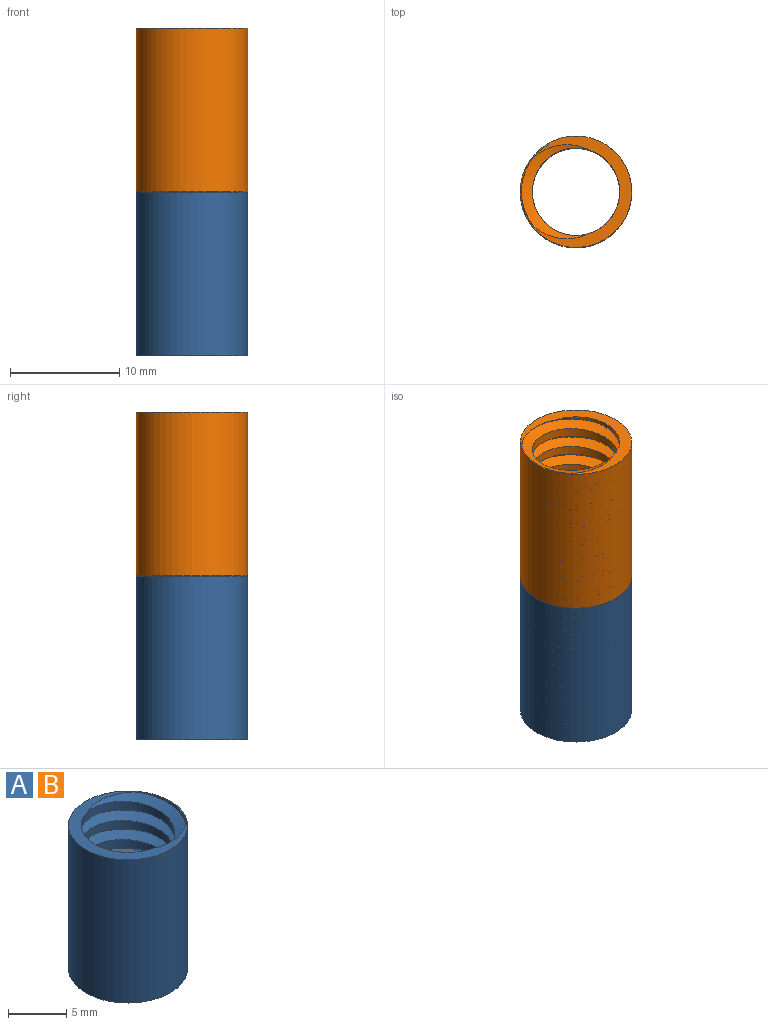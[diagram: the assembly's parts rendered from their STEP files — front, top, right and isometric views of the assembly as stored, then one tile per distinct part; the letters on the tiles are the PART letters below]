
ASSEMBLY  parts=2 mates=1
PART A: 7 faces, bbox 10.5x10.8x16.1 mm
  f0: cylinder r=4mm len=15mm, axis (0,0,1), area 157.5mm2, adj f2,f3,f4,f5
  f1: cylinder r=5.1mm len=15mm, axis (0,0,1), area 480.7mm2, adj f2,f3
  f2: plane 10.49x10.49mm, normal (0,0,-1), area 20.4mm2, adj f0,f1,f4,f5,f6
  f3: plane 10.49x10.49mm, normal (0,0,1), area 20.4mm2, adj f0,f1,f4,f5,f6
  f4: bspline ~15.8x10.51mm, area 236.2mm2, adj f0,f2,f3,f6
  f5: bspline ~15.8x10.51mm, area 236.1mm2, adj f0,f2,f3,f6
  f6: cylinder r=5mm len=15mm, axis (0,0,-1), area 105.4mm2, adj f2,f3,f4,f5
PART B: same geometry as A
PLACE A t=(4.05,-2.24,-0.87)mm fixed
PLACE B rot(axis=(0,0,1),180deg) t=(4.05,-2.24,14.13)mm
MATE fastened B.f0 <-> A.f0  axis (0,0,-1) through (4.05,-2.24,0.63)mm
